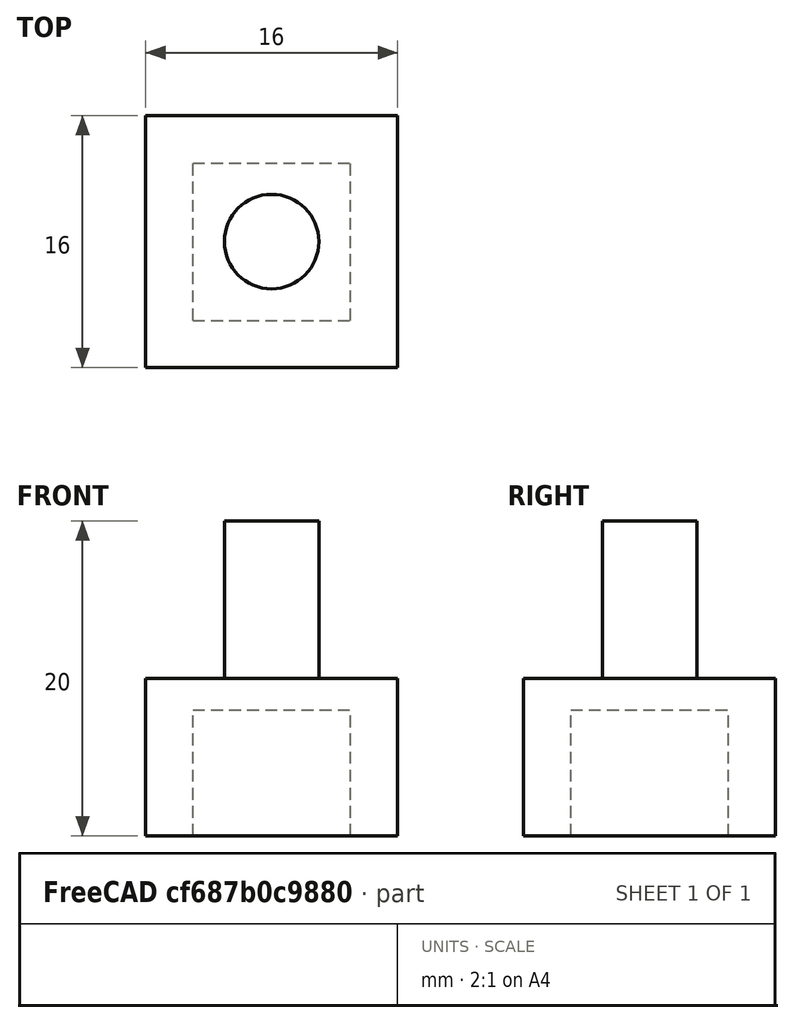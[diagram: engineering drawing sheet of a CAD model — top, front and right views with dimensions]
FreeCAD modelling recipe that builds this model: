
FCSTD DOCUMENT  (FreeCAD 0.18.3R)
Label: cylinder
License: All rights reserved
LicenseURL: http://en.wikipedia.org/wiki/All_rights_reserved
objects: Part::Box×2, Part::Cylinder×1, Part::Fuse×1, Part::Cut×1
note: 5 computed .brp shape members not serialized (recipe doc carries the construction recipe); baked Part::Feature solids carry a one-line shape summary decoded from their .brp

FEATURE [Part::Box] Box  label="Cube"
  AttacherType = Attacher::AttachEngine3D
  Height = 10
  Length = 16
  Placement = pos=(-8,-8,0) rot=(0,0,1;0rad)
  Width = 16
FEATURE [Part::Cylinder] Cylinder
  Angle = 360
  AttacherType = Attacher::AttachEngine3D
  Height = 10
  Placement = pos=(0,0,10) rot=(0,0,1;0rad)
  Radius = 3
FEATURE [Part::Fuse] Fusion
  Base = -> Box
  Tool = -> Cylinder
FEATURE [Part::Box] Box001  label="Cube001"
  AttacherType = Attacher::AttachEngine3D
  Height = 8
  Length = 10
  Placement = pos=(-5,-5,0) rot=(0,0,1;0rad)
  Width = 10
FEATURE [Part::Cut] Cut
  Base = -> Fusion
  Tool = -> Box001
